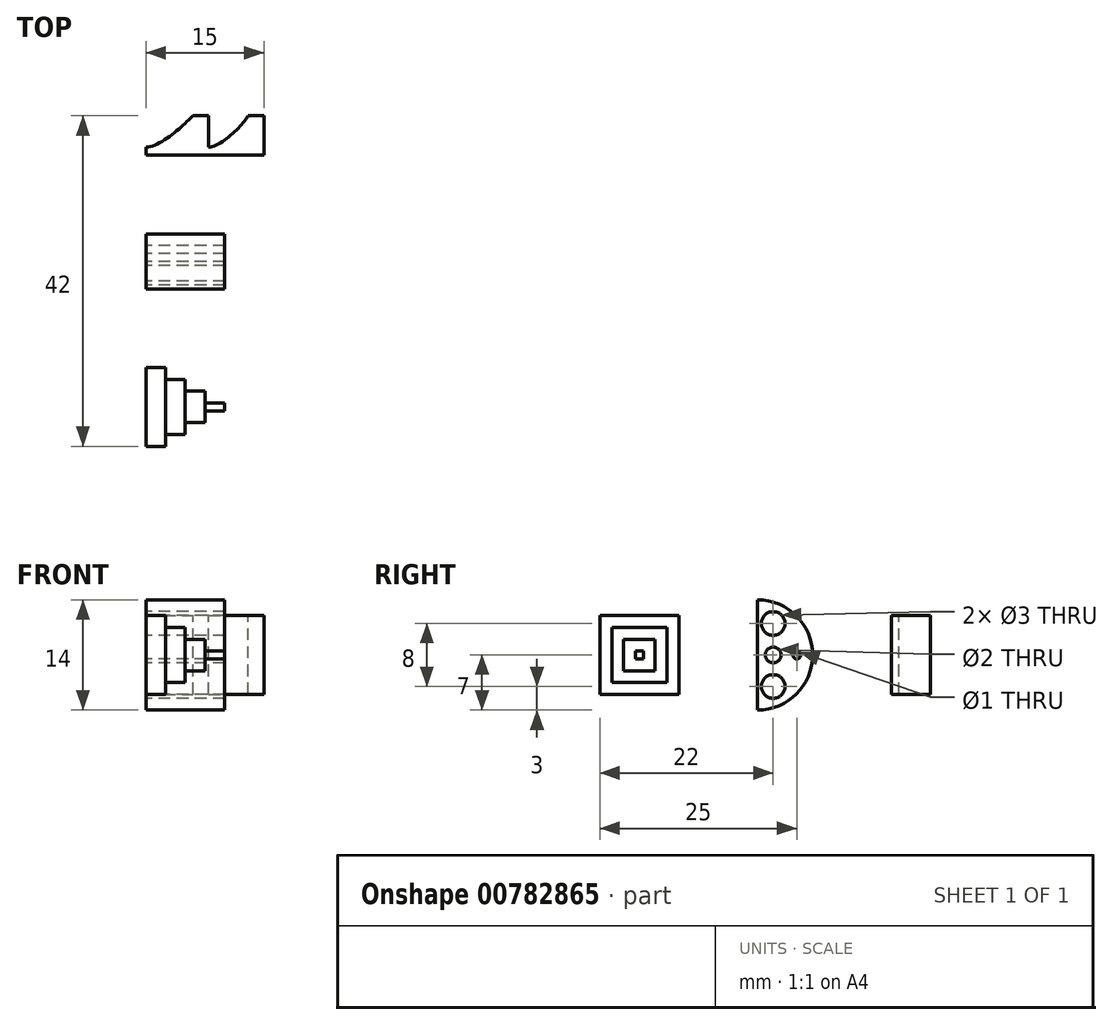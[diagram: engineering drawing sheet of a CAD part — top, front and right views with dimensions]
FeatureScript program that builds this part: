
annotation { "Feature Type Name" : "Feature", "Feature Type Description" : "" }
export const myFeature = defineFeature(function(context is Context, id is Id, definition is map)
    precondition{}
    {
        {
            var Q0;
            Q0=qCreatedBy(makeId("Right.planeOp"),FACE);
            var sketch = newSketch(context, id + "F0", { "sketchPlane" : qUnion([Q0])});
            skLineSegment(sketch, "E0", {"start": v(0, 0) * mm, "end": v(0, -14) * mm});
            skArc(sketch, "E1", {"start": v(0, -14) * mm, "mid": v(7, -7) * mm, "end": v(0, 0) * mm});
            skCircle(sketch, "E2", {"center": v(2, -3) * mm, "radius": 1.5 * mm});
            skCircle(sketch, "E3", {"center": v(2, -7) * mm, "radius": 1 * mm});
            skCircle(sketch, "E4", {"center": v(2, -11) * mm, "radius": 1.5 * mm});
            skCircle(sketch, "E5", {"center": v(5, -7) * mm, "radius": 0.5 * mm});
            skLineSegment(sketch, "E6.bottom", {"start": v(-10, -12) * mm, "end": v(-20, -12) * mm});
            skLineSegment(sketch, "E6.top", {"start": v(-10, -2) * mm, "end": v(-20, -2) * mm});
            skLineSegment(sketch, "E6.left", {"start": v(-10, -12) * mm, "end": v(-10, -2) * mm});
            skLineSegment(sketch, "E6.right", {"start": v(-20, -12) * mm, "end": v(-20, -2) * mm});
            skPoint(sketch, "E6.middle", {"position": v(-15, -7) * mm});
            skLineSegment(sketch, "E7.bottom", {"start": v(-11.5, -10.5) * mm, "end": v(-18.5, -10.5) * mm});
            skLineSegment(sketch, "E7.top", {"start": v(-11.5, -3.5) * mm, "end": v(-18.5, -3.5) * mm});
            skLineSegment(sketch, "E7.left", {"start": v(-11.5, -10.5) * mm, "end": v(-11.5, -3.5) * mm});
            skLineSegment(sketch, "E7.right", {"start": v(-18.5, -10.5) * mm, "end": v(-18.5, -3.5) * mm});
            skLineSegment(sketch, "E8.bottom", {"start": v(-13, -9) * mm, "end": v(-17, -9) * mm});
            skLineSegment(sketch, "E8.top", {"start": v(-13, -5) * mm, "end": v(-17, -5) * mm});
            skLineSegment(sketch, "E8.left", {"start": v(-13, -9) * mm, "end": v(-13, -5) * mm});
            skLineSegment(sketch, "E8.right", {"start": v(-17, -9) * mm, "end": v(-17, -5) * mm});
            skLineSegment(sketch, "E9.bottom", {"start": v(-14.5, -7.5) * mm, "end": v(-15.5, -7.5) * mm});
            skLineSegment(sketch, "E9.top", {"start": v(-14.5, -6.5) * mm, "end": v(-15.5, -6.5) * mm});
            skLineSegment(sketch, "E9.left", {"start": v(-14.5, -7.5) * mm, "end": v(-14.5, -6.5) * mm});
            skLineSegment(sketch, "E9.right", {"start": v(-15.5, -7.5) * mm, "end": v(-15.5, -6.5) * mm});
            skLineSegment(sketch, "E10.bottom", {"start": v(17, -2) * mm, "end": v(22, -2) * mm});
            skLineSegment(sketch, "E10.top", {"start": v(17, -12) * mm, "end": v(22, -12) * mm});
            skLineSegment(sketch, "E10.left", {"start": v(17, -2) * mm, "end": v(17, -12) * mm});
            skLineSegment(sketch, "E10.right", {"start": v(22, -2) * mm, "end": v(22, -12) * mm});
            skSolve(sketch);
        }
        {
            var Q0;
            Q0=makeQuery(id+"F0.imprint","IMPRINT",FACE,{"disambiguationData":[TD([[makeQuery(id+"F0.imprint","IMPRINT",EDGE,{"derivedFrom":sQuery(id+"F0.wireOp",EDGE,"E6.bottom")}),-1.0]])]});
            var Q1;
            Q1=makeQuery(id+"F0.imprint","IMPRINT",FACE,{"disambiguationData":[TD([[makeQuery(id+"F0.imprint","IMPRINT",EDGE,{"derivedFrom":sQuery(id+"F0.wireOp",EDGE,"E7.bottom")}),-1.0]])]});
            var Q2;
            Q2=makeQuery(id+"F0.imprint","IMPRINT",FACE,{"disambiguationData":[TD([[makeQuery(id+"F0.imprint","IMPRINT",EDGE,{"derivedFrom":sQuery(id+"F0.wireOp",EDGE,"E8.bottom")}),-1.0]])]});
            var Q3;
            Q3=makeQuery(id+"F0.imprint","IMPRINT",FACE,{"disambiguationData":[TD([[makeQuery(id+"F0.imprint","IMPRINT",EDGE,{"derivedFrom":sQuery(id+"F0.wireOp",EDGE,"E9.bottom")}),-1.0]])]});
            extrude(context, id + "F1", {"entities" : qUnion([Q0, Q1, Q2, Q3]), "depth" : 2.5 * mm, "offsetDistance" : 25 * mm});
        }
        {
            var Q0;
            Q0=makeQuery(id+"F0.imprint","IMPRINT",FACE,{"disambiguationData":[TD([[makeQuery(id+"F0.imprint","IMPRINT",EDGE,{"derivedFrom":sQuery(id+"F0.wireOp",EDGE,"E7.bottom")}),-1.0]])]});
            var Q1;
            Q1=makeQuery(id+"F0.imprint","IMPRINT",FACE,{"disambiguationData":[TD([[makeQuery(id+"F0.imprint","IMPRINT",EDGE,{"derivedFrom":sQuery(id+"F0.wireOp",EDGE,"E8.bottom")}),-1.0]])]});
            var Q2;
            Q2=makeQuery(id+"F0.imprint","IMPRINT",FACE,{"disambiguationData":[TD([[makeQuery(id+"F0.imprint","IMPRINT",EDGE,{"derivedFrom":sQuery(id+"F0.wireOp",EDGE,"E9.bottom")}),-1.0]])]});
            extrude(context, id + "F2", {"entities" : qUnion([Q0, Q1, Q2]), "operationType" : NewBodyOperationType.ADD, "depth" : 5 * mm, "hasOffset" : true, "offsetDistance" : 5 * mm});
        }
        {
            var Q0;
            Q0=makeQuery(id+"F0.imprint","IMPRINT",FACE,{"disambiguationData":[TD([[makeQuery(id+"F0.imprint","IMPRINT",EDGE,{"derivedFrom":sQuery(id+"F0.wireOp",EDGE,"E8.bottom")}),-1.0]])]});
            var Q1;
            Q1=makeQuery(id+"F0.imprint","IMPRINT",FACE,{"disambiguationData":[TD([[makeQuery(id+"F0.imprint","IMPRINT",EDGE,{"derivedFrom":sQuery(id+"F0.wireOp",EDGE,"E9.bottom")}),-1.0]])]});
            extrude(context, id + "F3", {"entities" : qUnion([Q0, Q1]), "operationType" : NewBodyOperationType.ADD, "depth" : 7.5 * mm, "offsetDistance" : 25 * mm});
        }
        {
            var Q0;
            Q0=makeQuery(id+"F0.imprint","IMPRINT",FACE,{"disambiguationData":[TD([[makeQuery(id+"F0.imprint","IMPRINT",EDGE,{"derivedFrom":sQuery(id+"F0.wireOp",EDGE,"E9.bottom")}),-1.0]])]});
            extrude(context, id + "F4", {"entities" : qUnion([Q0]), "operationType" : NewBodyOperationType.ADD, "depth" : 10 * mm, "offsetDistance" : 25 * mm});
        }
        {
            var Q0;
            Q0=makeQuery(id+"F0.imprint","IMPRINT",FACE,{"disambiguationData":[TD([[makeQuery(id+"F0.imprint","IMPRINT",EDGE,{"derivedFrom":sQuery(id+"F0.wireOp",EDGE,"E0")}),1.0]])]});
            extrude(context, id + "F5", {"entities" : qUnion([Q0]), "depth" : 10 * mm, "offsetDistance" : 25 * mm});
        }
        {
            var Q0;
            Q0=makeQuery(id+"F0.imprint","IMPRINT",FACE,{"disambiguationData":[TD([[makeQuery(id+"F0.imprint","IMPRINT",EDGE,{"derivedFrom":sQuery(id+"F0.wireOp",EDGE,"E10.bottom")}),-1.0]])]});
            extrude(context, id + "F6", {"entities" : qUnion([Q0]), "depth" : 15 * mm, "offsetDistance" : 25 * mm});
        }
        {
            var Q0;
            Q0=qCreatedBy(makeId("Top.planeOp"),FACE);
            var sketch = newSketch(context, id + "F7", { "sketchPlane" : qUnion([Q0])});
            skLineSegment(sketch, "E11", {"start": v(0, 18) * mm, "end": v(0, 22) * mm});
            skLineSegment(sketch, "E12", {"start": v(5.97, 22) * mm, "end": v(0, 22) * mm});
            skFitSpline(sketch, "E13", {"points": [v(0, 18) * mm, v(5.97, 22) * mm], "startDerivative": vector(6, 0) * mm, "endDerivative": vector(2.12, 2.12) * mm});
            skLineSegment(sketch, "E14", {"start": v(5.97, 22) * mm, "end": v(6.41, 22.44) * mm, "construction": true});
            skLineSegment(sketch, "E15", {"start": v(5.97, 22) * mm, "end": v(5.97, 24.02) * mm, "construction": true});
            skLineSegment(sketch, "E16", {"start": v(0, 22) * mm, "end": v(5.97, 22) * mm});
            skLineSegment(sketch, "E17", {"start": v(0, 18) * mm, "end": v(2.2, 18) * mm, "construction": true});
            skLineSegment(sketch, "E18", {"start": v(7.97, 22) * mm, "end": v(7.97, 18) * mm});
            skFitSpline(sketch, "E19", {"points": [v(7.97, 18) * mm, v(13, 22) * mm], "startDerivative": vector(5.04, 0) * mm, "endDerivative": vector(1.73, 3) * mm});
            skLineSegment(sketch, "E20", {"start": v(13, 22) * mm, "end": v(13.9, 23.55) * mm, "construction": true});
            skLineSegment(sketch, "E21", {"start": v(13, 22) * mm, "end": v(13, 23.63) * mm, "construction": true});
            skLineSegment(sketch, "E22", {"start": v(7.97, 22) * mm, "end": v(13, 22) * mm});
            skSolve(sketch);
        }
        {
            var Q0;
            Q0=makeQuery(id+"F7.imprint","IMPRINT",FACE,{"disambiguationData":[TD([[makeQuery(id+"F7.imprint","IMPRINT",EDGE,{"derivedFrom":sQuery(id+"F7.wireOp",EDGE,"E18")}),1.0]])]});
            var Q1;
            Q1=makeQuery(id+"F7.imprint","IMPRINT",FACE,{"disambiguationData":[TD([[makeQuery(id+"F7.imprint","IMPRINT",EDGE,{"derivedFrom":sQuery(id+"F7.wireOp",EDGE,"E11")}),-1.0]])]});
            extrude(context, id + "F8", {"entities" : qUnion([Q0, Q1]), "operationType" : NewBodyOperationType.REMOVE, "oppositeDirection" : true, "depth" : 25 * mm, "offsetDistance" : 25 * mm});
        }
    });
